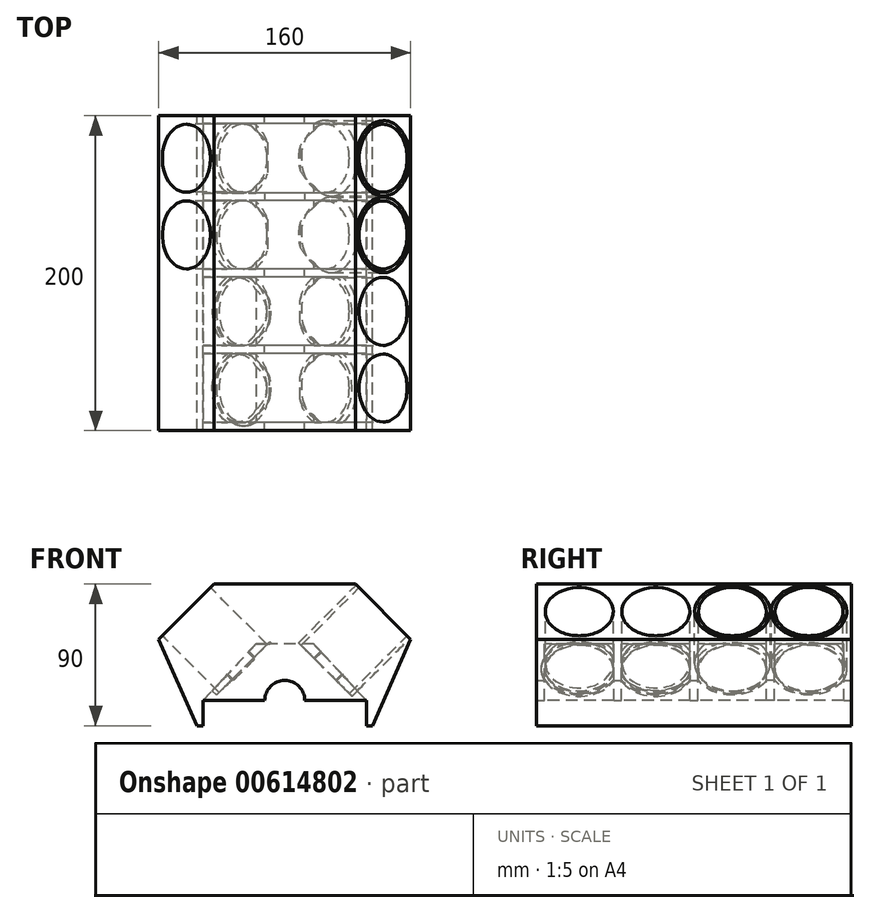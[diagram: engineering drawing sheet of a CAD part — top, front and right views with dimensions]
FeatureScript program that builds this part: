
annotation { "Feature Type Name" : "Feature", "Feature Type Description" : "" }
export const myFeature = defineFeature(function(context is Context, id is Id, definition is map)
    precondition{}
    {
        {
            var Q0;
            Q0=qCreatedBy(makeId("Front.planeOp"),FACE);
            var sketch = newSketch(context, id + "F0", { "sketchPlane" : qUnion([Q0])});
            skLineSegment(sketch, "E0", {"start": v(-55.67, -55) * mm, "end": v(55.67, -55) * mm});
            skLineSegment(sketch, "E1", {"start": v(55.67, -55) * mm, "end": v(80, 0) * mm});
            skLineSegment(sketch, "E2", {"start": v(80, 0) * mm, "end": v(45, 35) * mm});
            skLineSegment(sketch, "E3", {"start": v(45, 35) * mm, "end": v(-45, 35) * mm});
            skLineSegment(sketch, "E4.MirrorCS", {"start": v(-80, 0) * mm, "end": v(-45, 35) * mm});
            skLineSegment(sketch, "E5.MirrorCS", {"start": v(-55.67, -55) * mm, "end": v(-80, 0) * mm});
            skLineSegment(sketch, "E6.bottom", {"start": v(51.79, -55) * mm, "end": v(-51.79, -55) * mm});
            skLineSegment(sketch, "E6.top", {"start": v(51.79, -38.92) * mm, "end": v(-51.79, -38.92) * mm});
            skLineSegment(sketch, "E6.left", {"start": v(51.79, -55) * mm, "end": v(51.79, -38.92) * mm});
            skLineSegment(sketch, "E6.right", {"start": v(-51.79, -55) * mm, "end": v(-51.79, -38.92) * mm});
            skPoint(sketch, "E6.middle", {"position": v(0, -46.96) * mm});
            skLineSegment(sketch, "E7", {"start": v(51.79, -38.92) * mm, "end": v(18.4, -3.1) * mm});
            skLineSegment(sketch, "E8.MirrorCS", {"start": v(-51.79, -38.92) * mm, "end": v(-18.4, -3.1) * mm});
            skLineSegment(sketch, "E9", {"start": v(18.4, -3.1) * mm, "end": v(-18.4, -3.1) * mm});
            skPoint(sketch, "E10", {"position": v(0, -38.92) * mm});
            skCircle(sketch, "E11", {"center": v(0, -38.92) * mm, "radius": 12.7 * mm});
            skSolve(sketch);
        }
        {
            var Q0;
            {var subQ4=sQuery(id+"F0.wireOp",EDGE,"E1");Q0=makeQuery(id+"F0.imprint","IMPRINT",FACE,{"disambiguationData":[TD([[makeQuery(id+"F0.imprint","IMPRINT",EDGE,{"derivedFrom":subQ4}),1.0]])]});}
            var Q1;
            {var subQ0=sQuery(id+"F0.wireOp",EDGE,"E7");Q1=makeQuery(id+"F0.imprint","IMPRINT",FACE,{"disambiguationData":[TD([[makeQuery(id+"F0.imprint","IMPRINT",EDGE,{"derivedFrom":subQ0}),1.0]])]});}
            var Q2;
            Q2=makeQuery(id+"F0.imprint","IMPRINT",FACE,{"disambiguationData":[TD([[makeQuery(id+"F0.imprint","IMPRINT",EDGE,{"derivedFrom":sQuery(id+"F0.wireOp",EDGE,"E6.bottom")}),-1.0]])]});
            var Q3;
            Q3 = qSketchRegion(id + "F2", true);
            var Q4;
            {var subQ0=sQuery(id+"F0.wireOp",EDGE,"E6.top");var subQ1=sQuery(id+"F0.wireOp",EDGE,"ohakmxk2-f3Dc-bqEX-jLdr-mAi4omjDAJAe");var subQ2=makeQuery(id+"F0.imprint","INTERSECT",VERTEX,{"disambiguationData":[OD(0.0)],"derivedFrom":[subQ1,subQ0]});Q4=makeQuery(id+"F0.imprint","IMPRINT",FACE,{"disambiguationData":[TD([[makeQuery(id+"F0.imprint","IMPRINT",EDGE,{"disambiguationData":[TD([[subQ2,1.0]])],"derivedFrom":subQ1}),1.0]])]});}
            var Q5;
            {var subQ0=sQuery(id+"F0.wireOp",EDGE,"E6.top");var subQ1=sQuery(id+"F0.wireOp",EDGE,"ohakmxk2-f3Dc-bqEX-jLdr-mAi4omjDAJAe");var subQ2=makeQuery(id+"F0.imprint","INTERSECT",VERTEX,{"disambiguationData":[OD(0.0)],"derivedFrom":[subQ1,subQ0]});Q5=makeQuery(id+"F0.imprint","IMPRINT",FACE,{"disambiguationData":[TD([[makeQuery(id+"F0.imprint","IMPRINT",EDGE,{"disambiguationData":[TD([[subQ2,-1.0]])],"derivedFrom":subQ1}),1.0]])]});}
            extrude(context, id + "F1", {"entities" : qUnion([Q0, Q1, Q2, Q3, Q4, Q5]), "depth" : 200 * mm, "offsetDistance" : 25.4 * mm, "symmetric" : true});
        }
        {
            var Q0;
            Q0=makeQuery(id+"F1.opExtrude","SWEPT_FACE",FACE,{"disambiguationData":[OSD([sQuery(id+"F0.wireOp",EDGE,"E2")])]});
            var sketch = newSketch(context, id + "F2", { "sketchPlane" : qUnion([Q0])});
            skCircle(sketch, "E12", {"center": v(-24.32, -31.82) * mm, "radius": 21.59 * mm});
            skCircle(sketch, "E13", {"center": v(-72.95, -31.82) * mm, "radius": 21.59 * mm});
            skCircle(sketch, "E14.MirrorC", {"center": v(72.95, -31.82) * mm, "radius": 21.59 * mm});
            skCircle(sketch, "E15.MirrorC", {"center": v(24.32, -31.82) * mm, "radius": 21.59 * mm});
            skCircle(sketch, "E16", {"center": v(-72.95, -31.82) * mm, "radius": 24 * mm});
            skCircle(sketch, "E17", {"center": v(-24.32, -31.82) * mm, "radius": 24 * mm});
            skCircle(sketch, "E18", {"center": v(24.32, -31.82) * mm, "radius": 24 * mm});
            skCircle(sketch, "E19", {"center": v(72.95, -31.82) * mm, "radius": 24 * mm});
            skSolve(sketch);
        }
        {
            var Q0;
            Q0=makeQuery(id+"F1.opExtrude","SWEPT_FACE",FACE,{"disambiguationData":[OSD([sQuery(id+"F0.wireOp",EDGE,"E4.MirrorCS")])]});
            var sketch = newSketch(context, id + "F3", { "sketchPlane" : qUnion([Q0])});
            skCircle(sketch, "E20", {"center": v(-24.32, -31.81) * mm, "radius": 21.59 * mm});
            skCircle(sketch, "E21", {"center": v(-72.95, -31.83) * mm, "radius": 21.59 * mm});
            skCircle(sketch, "E22.MirrorC", {"center": v(72.95, -31.83) * mm, "radius": 21.59 * mm});
            skCircle(sketch, "E23.MirrorC", {"center": v(24.32, -31.83) * mm, "radius": 21.59 * mm});
            skCircle(sketch, "E24", {"center": v(24.32, -31.83) * mm, "radius": 24 * mm});
            skCircle(sketch, "E25", {"center": v(72.95, -31.83) * mm, "radius": 24 * mm});
            skCircle(sketch, "E26.MirrorC", {"center": v(-24.32, -31.83) * mm, "radius": 24 * mm});
            skCircle(sketch, "E27.MirrorC", {"center": v(-72.95, -31.83) * mm, "radius": 24 * mm});
            skSolve(sketch);
        }
        {
            var Q0;
            Q0=makeQuery(id+"F2.imprint","IMPRINT",FACE,{"disambiguationData":[TD([[makeQuery(id+"F2.imprint","IMPRINT",EDGE,{"derivedFrom":sQuery(id+"F2.wireOp",EDGE,"E14.MirrorC")}),-1.0]])]});
            var Q1;
            Q1=makeQuery(id+"F2.imprint","IMPRINT",FACE,{"disambiguationData":[TD([[makeQuery(id+"F2.imprint","IMPRINT",EDGE,{"derivedFrom":sQuery(id+"F2.wireOp",EDGE,"E15.MirrorC")}),-1.0]])]});
            var Q2;
            Q2=makeQuery(id+"F2.imprint","IMPRINT",FACE,{"disambiguationData":[TD([[makeQuery(id+"F2.imprint","IMPRINT",EDGE,{"derivedFrom":sQuery(id+"F2.wireOp",EDGE,"E12")}),1.0]])]});
            var Q3;
            Q3=makeQuery(id+"F2.imprint","IMPRINT",FACE,{"disambiguationData":[TD([[makeQuery(id+"F2.imprint","IMPRINT",EDGE,{"derivedFrom":sQuery(id+"F2.wireOp",EDGE,"E13")}),1.0]])]});
            extrude(context, id + "F4", {"entities" : qUnion([Q0, Q1, Q2, Q3]), "operationType" : NewBodyOperationType.REMOVE, "oppositeDirection" : true, "depth" : 52 * mm, "offsetDistance" : 25 * mm});
        }
        {
            var Q0;
            Q0=makeQuery(id+"F3.imprint","IMPRINT",FACE,{"disambiguationData":[TD([[makeQuery(id+"F3.imprint","IMPRINT",EDGE,{"derivedFrom":sQuery(id+"F3.wireOp",EDGE,"E21")}),1.0]])]});
            var Q1;
            Q1=makeQuery(id+"F3.imprint","IMPRINT",FACE,{"disambiguationData":[TD([[makeQuery(id+"F3.imprint","IMPRINT",EDGE,{"derivedFrom":sQuery(id+"F3.wireOp",EDGE,"E20")}),1.0]])]});
            var Q2;
            Q2=makeQuery(id+"F3.imprint","IMPRINT",FACE,{"disambiguationData":[TD([[makeQuery(id+"F3.imprint","IMPRINT",EDGE,{"derivedFrom":sQuery(id+"F3.wireOp",EDGE,"E23.MirrorC")}),-1.0]])]});
            var Q3;
            Q3=makeQuery(id+"F3.imprint","IMPRINT",FACE,{"disambiguationData":[TD([[makeQuery(id+"F3.imprint","IMPRINT",EDGE,{"derivedFrom":sQuery(id+"F3.wireOp",EDGE,"E22.MirrorC")}),-1.0]])]});
            var Q4;
            Q4 = qConstructionFilter(qBodyType(qCreatedBy(id + "F3" ,EDGE), BodyType.WIRE), ConstructionObject.NO);
            extrude(context, id + "F5", {"entities" : qUnion([Q0, Q1, Q2, Q3]), "operationType" : NewBodyOperationType.REMOVE, "surfaceEntities" : qUnion([Q4]), "oppositeDirection" : true, "depth" : 52 * mm, "offsetDistance" : 25 * mm});
        }
        {
            var Q0;
            {var subQ4=sQuery(id+"F0.wireOp",EDGE,"E7");Q0=makeQuery(id+"F0.imprint","IMPRINT",FACE,{"disambiguationData":[TD([[makeQuery(id+"F0.imprint","IMPRINT",EDGE,{"derivedFrom":subQ4}),1.0]])]});}
            extrude(context, id + "F6", {"entities" : qUnion([Q0]), "operationType" : NewBodyOperationType.ADD, "depth" : 5 * mm, "offsetDistance" : 25 * mm, "symmetric" : true});
        }
        {
            var Q0;
            {var subQ4=sQuery(id+"F0.wireOp",EDGE,"E7");Q0=makeQuery(id+"F0.imprint","IMPRINT",FACE,{"disambiguationData":[TD([[makeQuery(id+"F0.imprint","IMPRINT",EDGE,{"derivedFrom":subQ4}),1.0]])]});}
            var Q1;
            Q1=makeQuery(id+"F0.imprint","IMPRINT",FACE,{"disambiguationData":[TD([[makeQuery(id+"F0.imprint","IMPRINT",EDGE,{"derivedFrom":sQuery(id+"F0.wireOp",EDGE,"E6.bottom")}),-1.0]])]});
            extrude(context, id + "F7", {"entities" : qUnion([Q0, Q1]), "operationType" : NewBodyOperationType.REMOVE, "oppositeDirection" : true, "depth" : 190 * mm, "offsetDistance" : 25 * mm, "symmetric" : true});
        }
        {
            var Q0;
            {var subQ4=sQuery(id+"F0.wireOp",EDGE,"E7");Q0=makeQuery(id+"F0.imprint","IMPRINT",FACE,{"disambiguationData":[TD([[makeQuery(id+"F0.imprint","IMPRINT",EDGE,{"derivedFrom":subQ4}),1.0]])]});}
            extrude(context, id + "F8", {"entities" : qUnion([Q0]), "operationType" : NewBodyOperationType.ADD, "depth" : 5 * mm, "offsetDistance" : 25 * mm, "symmetric" : true});
        }
        {
            var Q0;
            Q0 = qSketchRegion(id + "F3", true);
            var Q1;
            Q1 = qConstructionFilter(qBodyType(qCreatedBy(id + "F3" ,EDGE), BodyType.WIRE), ConstructionObject.NO);
            extrude(context, id + "F9", {"entities" : qUnion([Q0]), "surfaceEntities" : qUnion([Q1]), "oppositeDirection" : true, "depth" : 51 * mm, "offsetDistance" : 25 * mm});
        }
        {
            var Q0;
            Q0=makeQuery(id+"F8.opExtrude","CAP_FACE",FACE,{"disambiguationData":[OSD([sQuery(id+"F0.wireOp",EDGE,"E6.top"),sQuery(id+"F0.wireOp",EDGE,"E7"),sQuery(id+"F0.wireOp",EDGE,"E8.MirrorCS"),sQuery(id+"F0.wireOp",EDGE,"E9"),sQuery(id+"F0.wireOp",EDGE,"E11")])],"isStart":false});
            extrude(context, id + "F10", {"entities" : qUnion([Q0]), "operationType" : NewBodyOperationType.ADD, "depth" : 48.5 * mm, "offsetDistance" : 25 * mm, "hasSecondDirection" : true, "secondDirectionOppositeDirection" : false, "secondDirectionDepth" : 43.5 * mm});
        }
        {
            var Q0;
            Q0=makeQuery(id+"F8.opExtrude","CAP_FACE",FACE,{"disambiguationData":[OSD([sQuery(id+"F0.wireOp",EDGE,"E6.top"),sQuery(id+"F0.wireOp",EDGE,"E7"),sQuery(id+"F0.wireOp",EDGE,"E8.MirrorCS"),sQuery(id+"F0.wireOp",EDGE,"E9"),sQuery(id+"F0.wireOp",EDGE,"E11")])],"isStart":true});
            extrude(context, id + "F11", {"entities" : qUnion([Q0]), "operationType" : NewBodyOperationType.ADD, "depth" : 48.5 * mm, "offsetDistance" : 25 * mm, "hasSecondDirection" : true, "secondDirectionOppositeDirection" : false, "secondDirectionDepth" : 43.5 * mm});
        }
        {
            var Q0;
            Q0=makeQuery(id+"F2.imprint","IMPRINT",FACE,{"disambiguationData":[TD([[makeQuery(id+"F2.imprint","IMPRINT",EDGE,{"derivedFrom":sQuery(id+"F2.wireOp",EDGE,"E13")}),-1.0]])]});
            var Q1;
            Q1=makeQuery(id+"F2.imprint","IMPRINT",FACE,{"disambiguationData":[TD([[makeQuery(id+"F2.imprint","IMPRINT",EDGE,{"derivedFrom":sQuery(id+"F2.wireOp",EDGE,"E12")}),-1.0]])]});
            var Q2;
            Q2=makeQuery(id+"F2.imprint","IMPRINT",FACE,{"disambiguationData":[TD([[makeQuery(id+"F2.imprint","IMPRINT",EDGE,{"derivedFrom":sQuery(id+"F2.wireOp",EDGE,"E15.MirrorC")}),1.0]])]});
            var Q3;
            Q3=makeQuery(id+"F2.imprint","IMPRINT",FACE,{"disambiguationData":[TD([[makeQuery(id+"F2.imprint","IMPRINT",EDGE,{"derivedFrom":sQuery(id+"F2.wireOp",EDGE,"E14.MirrorC")}),1.0]])]});
            extrude(context, id + "F12", {"entities" : qUnion([Q0, Q1, Q2, Q3]), "oppositeDirection" : true, "depth" : 52 * mm, "offsetDistance" : 25 * mm});
        }
        {
            var Q0;
            Q0=makeQuery(id+"F1.opExtrude","SWEPT_BODY",BODY,{"disambiguationData":[OSD([sQuery(id+"F0.wireOp",EDGE,"E0"),sQuery(id+"F0.wireOp",EDGE,"E1"),sQuery(id+"F0.wireOp",EDGE,"E2"),sQuery(id+"F0.wireOp",EDGE,"E3"),sQuery(id+"F0.wireOp",EDGE,"E4.MirrorCS"),sQuery(id+"F0.wireOp",EDGE,"E5.MirrorCS"),sQuery(id+"F0.wireOp",EDGE,"E6.bottom"),sQuery(id+"F0.wireOp",EDGE,"E11")])]});
            var Q1;
            Q1=makeQuery(id+"F9.opExtrude","SWEPT_BODY",BODY,{"disambiguationData":[OSD([sQuery(id+"F3.wireOp",EDGE,"E20"),sQuery(id+"F3.wireOp",EDGE,"E26.MirrorC")])]});
            var Q2;
            Q2=makeQuery(id+"F9.opExtrude","SWEPT_BODY",BODY,{"disambiguationData":[OSD([sQuery(id+"F3.wireOp",EDGE,"E21"),sQuery(id+"F3.wireOp",EDGE,"E27.MirrorC")])]});
            var Q3;
            Q3=makeQuery(id+"F9.opExtrude","SWEPT_BODY",BODY,{"disambiguationData":[OSD([sQuery(id+"F3.wireOp",EDGE,"E22.MirrorC"),sQuery(id+"F3.wireOp",EDGE,"E25")])]});
            var Q4;
            Q4=makeQuery(id+"F9.opExtrude","SWEPT_BODY",BODY,{"disambiguationData":[OSD([sQuery(id+"F3.wireOp",EDGE,"E23.MirrorC"),sQuery(id+"F3.wireOp",EDGE,"E24")])]});
            var Q5;
            Q5=makeQuery(id+"F12.opExtrude","SWEPT_BODY",BODY,{"disambiguationData":[OSD([sQuery(id+"F2.wireOp",EDGE,"E12"),sQuery(id+"F2.wireOp",EDGE,"E17")])]});
            var Q6;
            Q6=makeQuery(id+"F12.opExtrude","SWEPT_BODY",BODY,{"disambiguationData":[OSD([sQuery(id+"F2.wireOp",EDGE,"E13"),sQuery(id+"F2.wireOp",EDGE,"E16")])]});
            var Q7;
            Q7=makeQuery(id+"F12.opExtrude","SWEPT_BODY",BODY,{"disambiguationData":[OSD([sQuery(id+"F2.wireOp",EDGE,"E14.MirrorC"),sQuery(id+"F2.wireOp",EDGE,"E19")])]});
            var Q8;
            Q8=makeQuery(id+"F12.opExtrude","SWEPT_BODY",BODY,{"disambiguationData":[OSD([sQuery(id+"F2.wireOp",EDGE,"E15.MirrorC"),sQuery(id+"F2.wireOp",EDGE,"E18")])]});
            booleanBodies(context, id + "F13", {"operationType" : BooleanOperationType.UNION, "tools" : qUnion([Q0, Q1, Q2, Q3, Q4, Q5, Q6, Q7, Q8])});
        }
    });
